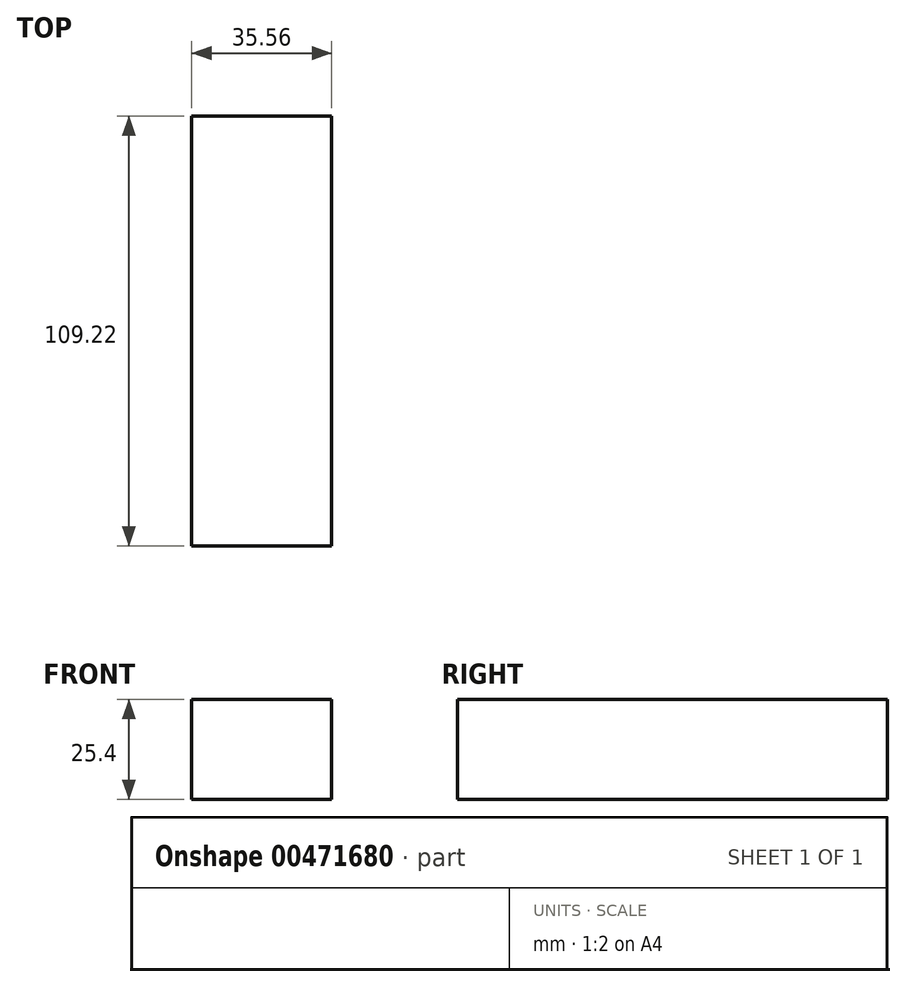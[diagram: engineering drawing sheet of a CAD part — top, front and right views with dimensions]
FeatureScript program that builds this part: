
annotation { "Feature Type Name" : "Feature", "Feature Type Description" : "" }
export const myFeature = defineFeature(function(context is Context, id is Id, definition is map)
    precondition{}
    {
        {
            var Q0;
            Q0=qCreatedBy(makeId("Top.planeOp"),FACE);
            var sketch = newSketch(context, id + "F0", { "sketchPlane" : qUnion([Q0])});
            skLineSegment(sketch, "E0.bottom", {"start": v(-17.78, 54.61) * mm, "end": v(17.78, 54.6) * mm});
            skLineSegment(sketch, "E0.top", {"start": v(-17.78, -54.6) * mm, "end": v(17.78, -54.61) * mm});
            skLineSegment(sketch, "E0.left", {"start": v(-17.78, 54.6) * mm, "end": v(-17.78, -54.6) * mm});
            skLineSegment(sketch, "E0.right", {"start": v(17.78, 54.6) * mm, "end": v(17.78, -54.6) * mm});
            skSolve(sketch);
        }
        {
            var Q0;
            Q0 = qSketchRegion(id + "F0", true);
            extrude(context, id + "F1", {"entities" : qUnion([Q0]), "depth" : 25.4 * mm});
        }
        {
            var Q0;
            Q0=makeQuery(id+"F1.opExtrude","SWEPT_FACE",FACE,{"disambiguationData":[OSD([sQuery(id+"F0.wireOp",EDGE,"E0.bottom")])]});
            var sketch = newSketch(context, id + "F2", { "sketchPlane" : qUnion([Q0])});
            skCircle(sketch, "E1", {"center": v(-12.94, 3.99) * mm, "radius": 1.27 * mm});
            skCircle(sketch, "E2", {"center": v(-9.68, 3.99) * mm, "radius": 1.27 * mm});
            skLineSegment(sketch, "E3.bottom", {"start": v(-12.94, 3.99) * mm, "end": v(-9.68, 3.99) * mm, "construction": true});
            skLineSegment(sketch, "E3.top", {"start": v(-12.94, 0) * mm, "end": v(-9.68, 0) * mm, "construction": true});
            skLineSegment(sketch, "E3.left", {"start": v(-12.94, 3.99) * mm, "end": v(-12.94, 0) * mm, "construction": true});
            skLineSegment(sketch, "E3.right", {"start": v(-9.68, 3.99) * mm, "end": v(-9.68, 0) * mm, "construction": true});
            skSolve(sketch);
        }
        {
            var Q0;
            Q0=sQuery(id+"F2.wireOp",EDGE,"E1");
            var Q1;
            Q1=sQuery(id+"F2.wireOp",EDGE,"E2");
            extrude(context, id + "F3", {"bodyType" : ToolBodyType.SURFACE, "surfaceEntities" : qUnion([Q0, Q1]), "depth" : 11.43 * mm});
        }
    });
